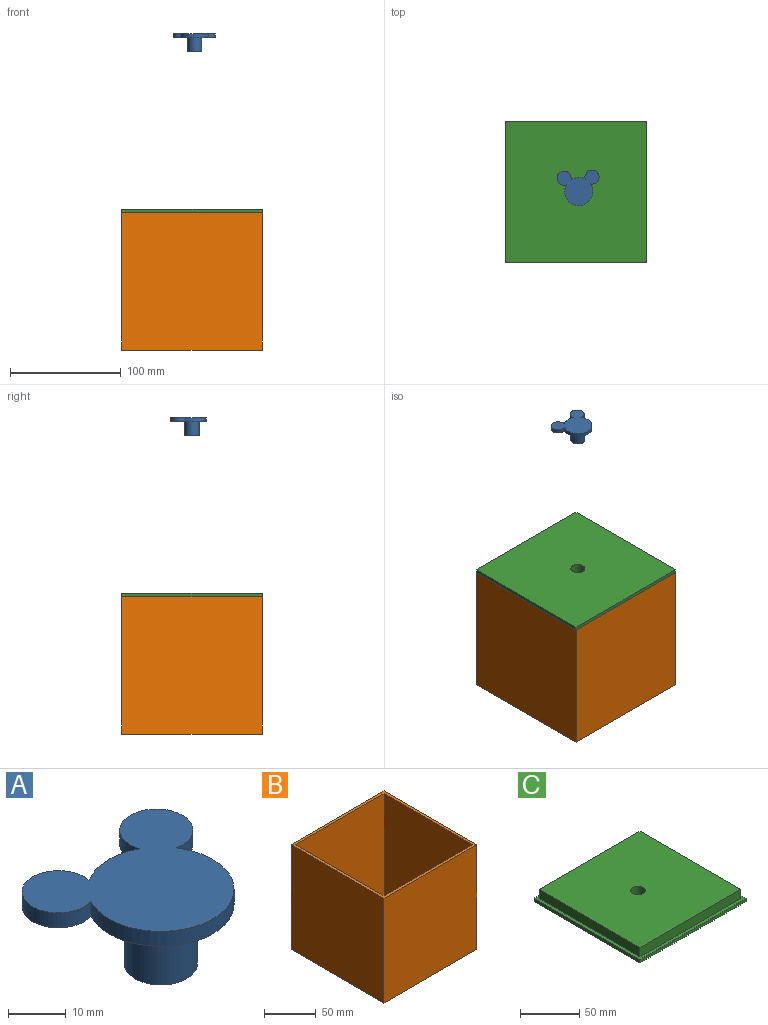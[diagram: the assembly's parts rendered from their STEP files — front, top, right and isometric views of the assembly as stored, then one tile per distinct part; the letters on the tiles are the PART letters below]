
ASSEMBLY  parts=3 mates=4
PART A: 8 faces, bbox 37.8x32.2x15.9 mm
  f0: cylinder r=6.35mm len=12.7mm, axis (0,0,1), area 506.7mm2, adj f1,f7
  f1: plane 12.7x12.7mm, normal (0,0,-1), area 126.7mm2, adj f0
  f2: cylinder r=6.35mm len=12.7mm, axis (0,0,-1), area 105.4mm2, adj f3,f5,f6,f7
  f3: cylinder r=12.7mm len=25.4mm, axis (0,0,-1), area 169.5mm2, adj f2,f4,f6,f7
  f4: cylinder r=6.35mm len=12.7mm, axis (0,0,-1), area 105.4mm2, adj f3,f5,f6,f7
  f5: cylinder r=12.7mm len=12.85mm, axis (0,0,-1), area 42.8mm2, adj f2,f4,f6,f7
  f6: plane 37.82x32.16mm, normal (0,0,1), area 749.1mm2, adj f2,f3,f4,f5
  f7: plane 37.82x32.16mm, normal (0,0,-1), area 622.5mm2, adj f0,f2,f3,f4,f5
PART B: 11 faces, bbox 127x127x123.8 mm
  f0: plane 127x123.83mm, normal (0,1,0), area 15725.8mm2, adj f1,f3,f4,f9
  f1: plane 127x123.83mm, normal (-1,0,0), area 15725.8mm2, adj f0,f2,f4,f9
  f2: plane 127x123.83mm, normal (0,-1,0), area 15725.8mm2, adj f1,f3,f4,f9
  f3: plane 127x123.83mm, normal (1,0,0), area 15725.8mm2, adj f0,f2,f4,f9
  f4: plane 127x127mm, normal (0,0,-1), area 16129mm2, adj f0,f1,f2,f3
  f5: plane 120.65x120.65mm, normal (1,0,0), area 14556.4mm2, adj f6,f8,f9,f10
  f6: plane 120.65x120.65mm, normal (0,-1,0), area 14556.4mm2, adj f5,f7,f9,f10
  f7: plane 120.65x120.65mm, normal (-1,0,0), area 14556.4mm2, adj f6,f8,f9,f10
  f8: plane 120.65x120.65mm, normal (0,1,0), area 14556.4mm2, adj f5,f7,f9,f10
  f9: plane 127x127mm, normal (0,0,1), area 1572.6mm2, adj f0,f1,f2,f3,f5,f6,f7,f8
  f10: plane 120.65x120.65mm, normal (0,0,1), area 14556.4mm2, adj f5,f6,f7,f8
PART C: 12 faces, bbox 127x127x12.7 mm
  f0: plane 120.65x9.53mm, normal (0,1,0), area 1149.2mm2, adj f1,f3,f4,f9
  f1: plane 120.65x9.53mm, normal (-1,0,0), area 1149.2mm2, adj f0,f2,f4,f9
  f2: plane 120.65x9.53mm, normal (0,-1,0), area 1149.2mm2, adj f1,f3,f4,f9
  f3: plane 120.65x9.53mm, normal (1,0,0), area 1149.2mm2, adj f0,f2,f4,f9
  f4: plane 120.65x120.65mm, normal (0,0,1), area 14429.7mm2, adj f0,f1,f2,f3,f11
  f5: plane 127x3.18mm, normal (0,1,0), area 403.2mm2, adj f6,f8,f9,f10
  f6: plane 127x3.18mm, normal (-1,0,0), area 403.2mm2, adj f5,f7,f9,f10
  f7: plane 127x3.18mm, normal (0,-1,0), area 403.2mm2, adj f6,f8,f9,f10
  f8: plane 127x3.18mm, normal (1,0,0), area 403.2mm2, adj f5,f7,f9,f10
  f9: plane 127x127mm, normal (0,0,1), area 1572.6mm2, adj f0,f1,f2,f3,f5,f6,f7,f8
  f10: plane 127x127mm, normal (0,0,-1), area 16002.3mm2, adj f5,f6,f7,f8,f11
  f11: cylinder r=6.35mm len=12.7mm, axis (0,0,-1), area 506.7mm2, adj f4,f10
PLACE A t=(2.44,84.98,139.82)mm
PLACE B t=(0,84.98,-142.24)mm
PLACE C rot(axis=(0,1,0),180deg) t=(2.44,84.98,-15.24)mm
MATE slider A.f0 <-> C.f11  axis (0,0,-1) through (2.44,84.98,127.12)mm
MATE planar C.f3 <-> B.f5  axis (-1,0,0) through (-60.33,84.98,-23.18)mm
MATE planar C.f2 <-> B.f8  axis (0,-1,0) through (0,24.65,-23.18)mm
MATE planar C.f9 <-> B.f9  axis (0,0,-1) through (0,84.98,-18.42)mm
